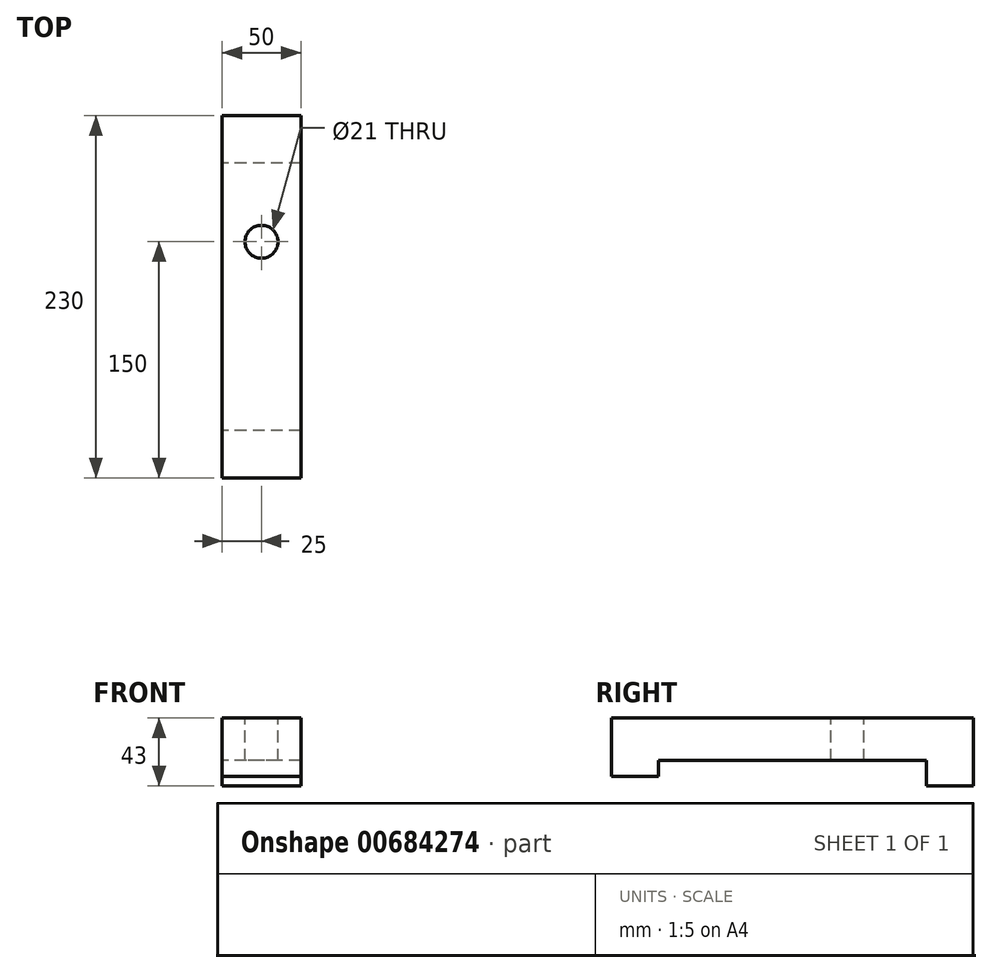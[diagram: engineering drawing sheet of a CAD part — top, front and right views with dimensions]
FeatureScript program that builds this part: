
annotation { "Feature Type Name" : "Feature", "Feature Type Description" : "" }
export const myFeature = defineFeature(function(context is Context, id is Id, definition is map)
    precondition{}
    {
        {
            var Q0;
            Q0=qCreatedBy(makeId("Top.planeOp"),FACE);
            var sketch = newSketch(context, id + "F0", { "sketchPlane" : qUnion([Q0])});
            skLineSegment(sketch, "E0.bottom", {"start": v(-25, 115) * mm, "end": v(25, 115) * mm});
            skLineSegment(sketch, "E0.top", {"start": v(-25, -115) * mm, "end": v(25, -115) * mm});
            skLineSegment(sketch, "E0.left", {"start": v(-25, 115) * mm, "end": v(-25, -115) * mm});
            skLineSegment(sketch, "E0.right", {"start": v(25, 115) * mm, "end": v(25, -115) * mm});
            skPoint(sketch, "E0.middle", {"position": v(0, 0) * mm});
            skSolve(sketch);
        }
        {
            var Q0;
            Q0=makeQuery(id+"F0.imprint","IMPRINT",FACE,{"disambiguationData":[TD([[makeQuery(id+"F0.imprint","IMPRINT",EDGE,{"derivedFrom":sQuery(id+"F0.wireOp",EDGE,"E0.bottom")}),-1.0]])]});
            extrude(context, id + "F1", {"entities" : qUnion([Q0]), "depth" : 27 * mm, "offsetDistance" : 25 * mm});
        }
        {
            var Q0;
            Q0=makeQuery(id+"F1.opExtrude","SWEPT_FACE",FACE,{"disambiguationData":[OSD([sQuery(id+"F0.wireOp",EDGE,"E0.left")])]});
            var sketch = newSketch(context, id + "F2", { "sketchPlane" : qUnion([Q0])});
            skLineSegment(sketch, "E1.0.0", {"start": v(115, 0) * mm, "end": v(-115, 0) * mm});
            skLineSegment(sketch, "E1.0.2", {"start": v(-115, 0) * mm, "end": v(115, 0) * mm});
            skLineSegment(sketch, "E2.bottom", {"start": v(-115, 0) * mm, "end": v(-85, 0) * mm});
            skLineSegment(sketch, "E2.top", {"start": v(-115, -16) * mm, "end": v(-85, -16) * mm});
            skLineSegment(sketch, "E2.left", {"start": v(-115, 0) * mm, "end": v(-115, -16) * mm});
            skLineSegment(sketch, "E2.right", {"start": v(-85, 0) * mm, "end": v(-85, -16) * mm});
            skLineSegment(sketch, "E3.bottom", {"start": v(115, 0) * mm, "end": v(85, 0) * mm});
            skLineSegment(sketch, "E3.top", {"start": v(115, -10) * mm, "end": v(85, -10) * mm});
            skLineSegment(sketch, "E3.left", {"start": v(115, 0) * mm, "end": v(115, -10) * mm});
            skLineSegment(sketch, "E3.right", {"start": v(85, 0) * mm, "end": v(85, -10) * mm});
            skSolve(sketch);
        }
        {
            var Q0;
            Q0=qSketchRegion(id+"F2",true);
            var Q1;
            Q1=makeQuery(id+"F1.opExtrude","SWEPT_FACE",FACE,{"disambiguationData":[OSD([sQuery(id+"F0.wireOp",EDGE,"E0.right")])]});
            extrude(context, id + "F3", {"entities" : qUnion([Q0]), "operationType" : NewBodyOperationType.ADD, "endBound" : BoundingType.UP_TO_SURFACE, "oppositeDirection" : true, "depth" : 25 * mm, "endBoundEntityFace" : qUnion([Q1]), "offsetDistance" : 25 * mm});
        }
        {
            var Q0;
            Q0=makeQuery(id+"F1.opExtrude","CAP_FACE",FACE,{"disambiguationData":[OSD([sQuery(id+"F0.wireOp",EDGE,"E0.bottom"),sQuery(id+"F0.wireOp",EDGE,"E0.top"),sQuery(id+"F0.wireOp",EDGE,"E0.left"),sQuery(id+"F0.wireOp",EDGE,"E0.right")])],"isStart":false});
            var sketch = newSketch(context, id + "F4", { "sketchPlane" : qUnion([Q0])});
            skLineSegment(sketch, "E4.0", {"start": v(-25, 115) * mm, "end": v(25, 115) * mm});
            skLineSegment(sketch, "E5.0", {"start": v(-25, -115) * mm, "end": v(25, -115) * mm});
            skLineSegment(sketch, "E6", {"start": v(0, 115) * mm, "end": v(0, -115) * mm});
            skPoint(sketch, "E7", {"position": v(0, 35) * mm});
            skSolve(sketch);
        }
        {
            var Q0;
            Q0=sQuery(id+"F4.wireOp",VERTEX,"E7");
            var Q1;
            Q1=makeQuery(id+"F1.opExtrude","SWEPT_BODY",BODY,{"disambiguationData":[OSD([sQuery(id+"F0.wireOp",EDGE,"E0.bottom"),sQuery(id+"F0.wireOp",EDGE,"E0.top"),sQuery(id+"F0.wireOp",EDGE,"E0.left"),sQuery(id+"F0.wireOp",EDGE,"E0.right")])]});
            hole(context, id + "F5", {"style" : HoleStyle.SIMPLE, "endStyle" : HoleEndStyle.THROUGH, "holeDiameter" : 21 * mm, "majorDiameter" : 5 * mm, "isTappedThrough" : true, "tappedDepth" : 12 * mm, "tapClearance" : 3, "locations" : qUnion([Q0]), "scope" : qUnion([Q1])});
        }
    });
